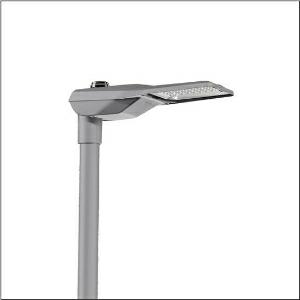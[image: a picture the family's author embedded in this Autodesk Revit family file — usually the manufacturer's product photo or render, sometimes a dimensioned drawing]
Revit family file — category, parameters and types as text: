
# Revit family: streetlight_sl_21_mini___p0_8a_5xe6u67n08jb_e378
name_source: partatom
category: Lighting Fixtures
units: mm (PartAtom-declared; Revit-internal decimal feet)

## family parameters
Cut with Voids When Loaded = No
Host = Face
Light Source = No
Part Type = Normal
Room Calculation Point = No
Round Connector Dimension = Use Diameter
Shared = No

## types (1)
- --- (1 x LED, 11600 lm, 87.3 W, 2700K)
    Apparent Load = 87 VA
    CIE Flux Codes = 36 69 97 100 100
    Color Rendering = 70
    Color Temperature = 2700K
    Default Elevation = 1800 mm
    Description = Streetlight SL 21 mini, mast luminaire, primary light control with lens, of PMMA, primary optical cover: cover, of toughened safety glass, transparent, light distribution: P0.8a, light emission: direct distribution, primary light characteristic: asymmetric, installation type: side-entry, LED, 3G 2.5mm², High Power LED, rated luminous flux: 11.600lm, luminous efficacy: 133lm/W, light colour: 727, colour temperature: 2700K, control gear: NEMA (7pin), control: flexible luminous flux parameterisation, time-dependent luminous flux control, constant luminous flux control, pre-setting: linear dimming characteristic, overheat protection, mains connection: 230..240V, AC, 50/60Hz, connection cable pre-assembled, cable length: 10,5m, wiring characteristics: H05VV-F, start of lifetime: 87W, end of service life: 90W, reduction: 40W, luminaire housing, of diecast aluminium (EN AC-44300), powder-coated, Siteco® metallic grey (DB 702S), corrosivity category C5 mid according to DIN EN ISO 12944, multi-level sealing system, sealing non-destructively replaceable, inclination adjustable: 0°, 5°, 10°, 15°, length: 628mm, width: 235mm, height: 110mm, spigot size: 42mm (side-entry), mounting height: 4..8m, protection rating (complete): IP66, insulation class (complete): insulation class I (protective earthing), certification: CE, ENEC, ENEC+, VDE, impact resistance: IK09, permissible operating ambient temperature for outdoor applications: -40..+50°C, standard-compliant lighting for roads and squares, packaging unit: 1 piece

Light Distribution: P0.8a
    Height = 110 mm
    Lamp = 1 x LED
    Lamp Light Flux = 11600 lm
    Lamp Power = 87.3 W
    Lamp count = 1
    Length = 625 mm
    Luminous efficacy = 133 lm/W
    Manufacturer = Siteco
    ModVariant = No
    Model = 5XE6U67N08JB
    Number of Poles = 1
    OnlyDefault = Yes
    Power Factor = 1
    Product Name = Streetlight SL 21 mini | P0.8a
    Product group = mast luminaire | pylon top
    ProductGroupID = 6100
    Protection Class = Protection class I
    Protection Degree = IP 66
    RLX_Detail_Level = 1
    RLX_Emergency_Light_Flux = 0 lm
    RLX_Emergency_Type = 0
    RLX_Emergency_Type_DB = No
    RlxData = <blob elided: 91981 chars, md5=8d4e137f>
    Socket = socket
    Standby Power = 0 W
    System Light Flux = 11600 lm
    System Power = 87 W
    Type Comments = factory setting: luminous flux: 100 % | dim-lin: 254 | 915 mA
    Type Image = l_1294379.jpg
    URL = http://relux.com
    VarID = @adj_068792
    Voltage = 0 V
    Weight = 0.00 kg
    Width = 234 mm

## geometry (parser evidence)
native form markers: Blend x4, Sweep x9
no freeform markers — native parametric forms only
